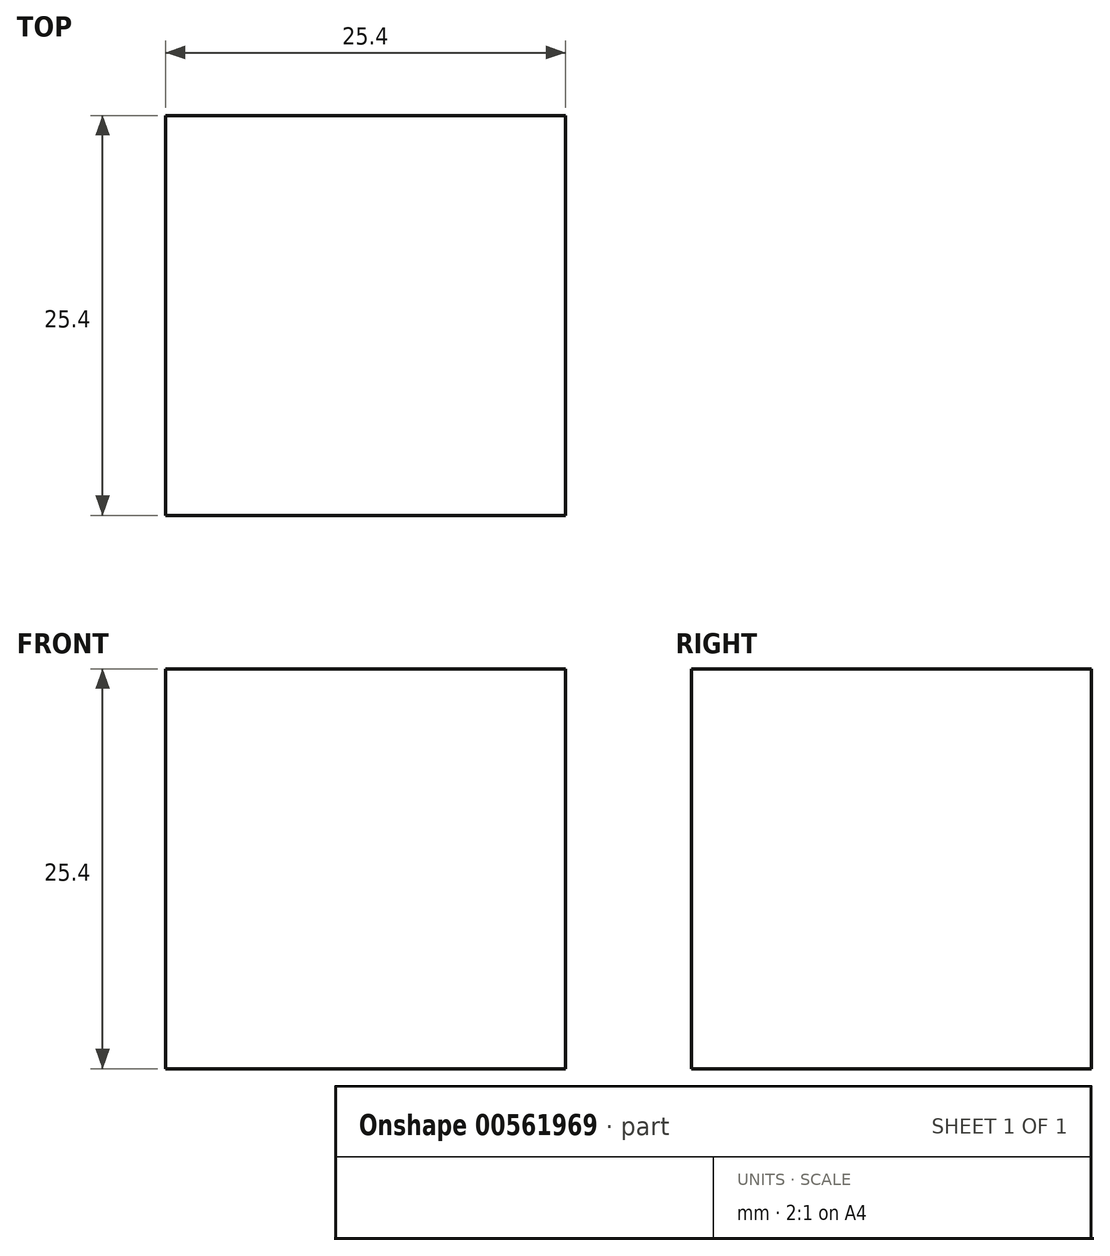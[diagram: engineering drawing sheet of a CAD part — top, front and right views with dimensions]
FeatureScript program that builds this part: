
annotation { "Feature Type Name" : "Feature", "Feature Type Description" : "" }
export const myFeature = defineFeature(function(context is Context, id is Id, definition is map)
    precondition{}
    {
        {
            var Q0;
            Q0=qCreatedBy(makeId("Front.planeOp"),FACE);
            var sketch = newSketch(context, id + "F0", { "sketchPlane" : qUnion([Q0])});
            skLineSegment(sketch, "E0.bottom", {"start": v(-57.85, 51.58) * mm, "end": v(-32.45, 51.58) * mm});
            skLineSegment(sketch, "E0.top", {"start": v(-57.85, 26.18) * mm, "end": v(-32.45, 26.18) * mm});
            skLineSegment(sketch, "E0.left", {"start": v(-57.85, 51.58) * mm, "end": v(-57.85, 26.18) * mm});
            skLineSegment(sketch, "E0.right", {"start": v(-32.45, 51.58) * mm, "end": v(-32.45, 26.18) * mm});
            skSolve(sketch);
        }
        {
            var Q0;
            Q0=makeQuery(id+"F0.imprint","IMPRINT",FACE,{"disambiguationData":[TD([[makeQuery(id+"F0.imprint","IMPRINT",EDGE,{"derivedFrom":sQuery(id+"F0.wireOp",EDGE,"E0.bottom")}),-1.0]])]});
            extrude(context, id + "F1", {"entities" : qUnion([Q0]), "depth" : 25.4 * mm, "offsetDistance" : 25.4 * mm});
        }
    });
